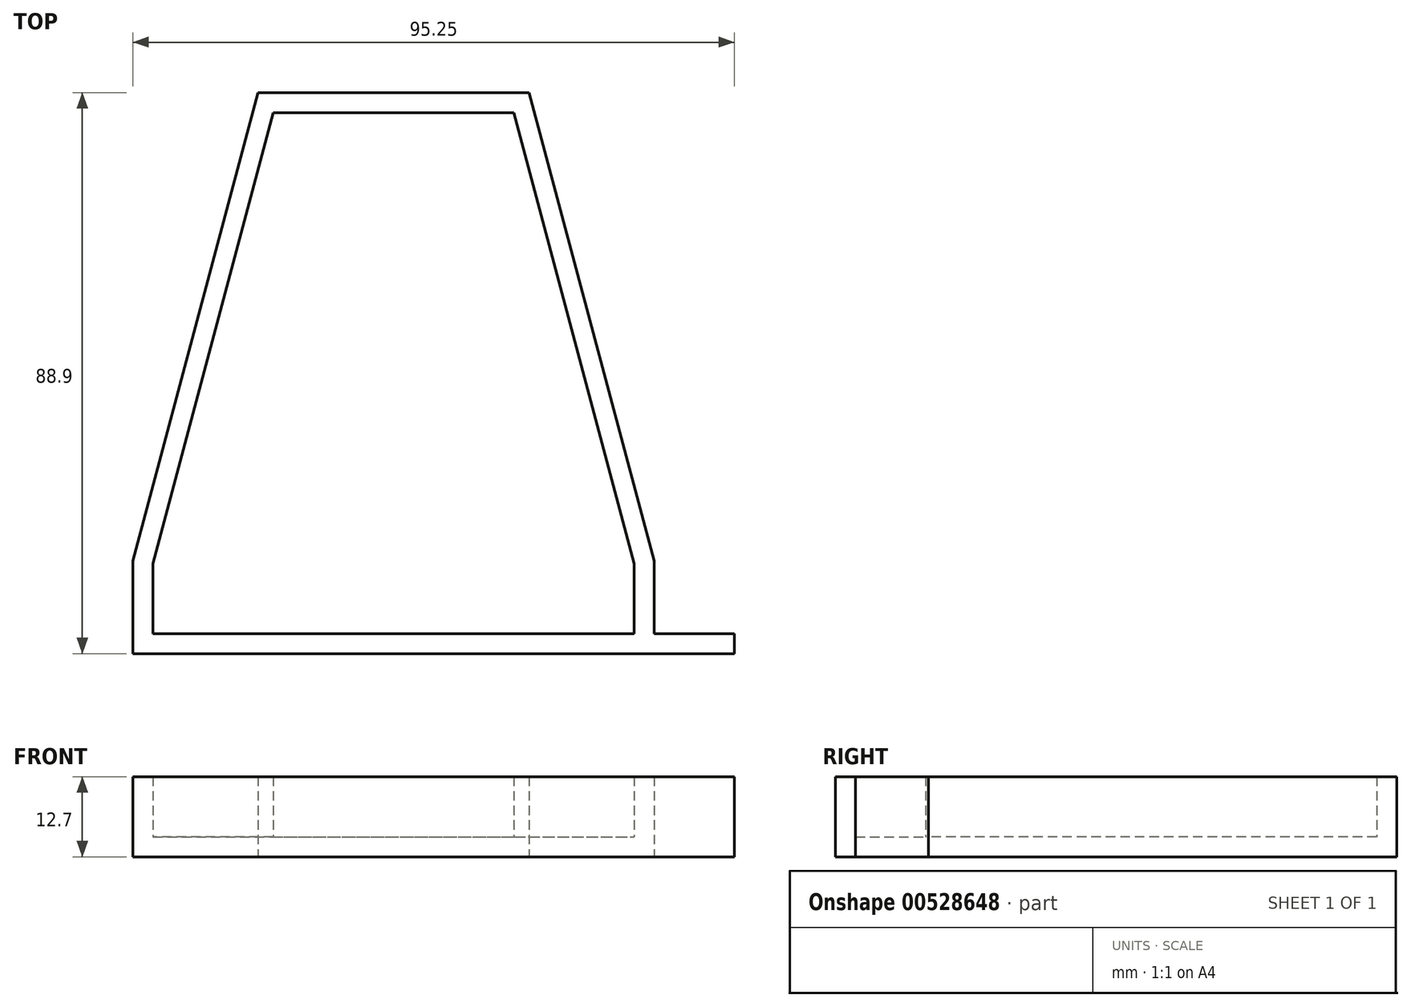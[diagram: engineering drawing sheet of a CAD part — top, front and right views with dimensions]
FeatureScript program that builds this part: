
annotation { "Feature Type Name" : "Feature", "Feature Type Description" : "" }
export const myFeature = defineFeature(function(context is Context, id is Id, definition is map)
    precondition{}
    {
        {
            var Q0;
            Q0=qCreatedBy(makeId("Top.planeOp"),FACE);
            var sketch = newSketch(context, id + "F0", { "sketchPlane" : qUnion([Q0])});
            skLineSegment(sketch, "E0.top", {"start": v(-38.1, -41.28) * mm, "end": v(38.1, -41.27) * mm});
            skLineSegment(sketch, "E1", {"start": v(38.1, -41.28) * mm, "end": v(38.1, -30.16) * mm});
            skLineSegment(sketch, "E2", {"start": v(19.05, 41.28) * mm, "end": v(38.1, -30.16) * mm});
            skLineSegment(sketch, "E3.MirrorCS", {"start": v(-19.05, 41.28) * mm, "end": v(-38.1, -30.16) * mm});
            skLineSegment(sketch, "E4.MirrorCS", {"start": v(-38.1, -41.28) * mm, "end": v(-38.1, -30.16) * mm});
            skLineSegment(sketch, "E5", {"start": v(-19.05, 41.27) * mm, "end": v(19.05, 41.28) * mm});
            skSolve(sketch);
        }
        {
            var Q0;
            Q0=makeQuery(id+"F0.imprint","IMPRINT",FACE,{"disambiguationData":[TD([[makeQuery(id+"F0.imprint","IMPRINT",EDGE,{"derivedFrom":sQuery(id+"F0.wireOp",EDGE,"E0.top")}),1.0]])]});
            var sketch = newSketch(context, id + "F1", { "sketchPlane" : qUnion([Q0])});
            skLineSegment(sketch, "E6.0", {"start": v(-21.49, 44.45) * mm, "end": v(-41.27, -29.75) * mm});
            skLineSegment(sketch, "E6.1", {"start": v(21.49, 44.45) * mm, "end": v(41.27, -29.75) * mm});
            skLineSegment(sketch, "E6.2", {"start": v(41.27, -44.45) * mm, "end": v(41.27, -29.75) * mm});
            skLineSegment(sketch, "E6.3", {"start": v(-21.49, 44.45) * mm, "end": v(21.49, 44.45) * mm});
            skLineSegment(sketch, "E6.4", {"start": v(-41.27, -44.45) * mm, "end": v(41.28, -44.45) * mm});
            skLineSegment(sketch, "E6.5", {"start": v(-41.27, -44.45) * mm, "end": v(-41.27, -29.75) * mm});
            skSolve(sketch);
        }
        {
            var Q0;
            Q0=makeQuery(id+"F0.imprint","IMPRINT",FACE,{"disambiguationData":[TD([[makeQuery(id+"F0.imprint","IMPRINT",EDGE,{"derivedFrom":sQuery(id+"F0.wireOp",EDGE,"E0.top")}),1.0]])]});
            extrude(context, id + "F2", {"entities" : qUnion([Q0]), "depth" : 3.17 * mm, "offsetDistance" : 25.4 * mm});
        }
        {
            var Q0;
            Q0=makeQuery(id+"F1.imprint","IMPRINT",FACE,{"disambiguationData":[TD([[makeQuery(id+"F1.imprint","IMPRINT",EDGE,{"derivedFrom":sQuery(id+"F1.wireOp",EDGE,"E6.0")}),1.0]])]});
            extrude(context, id + "F3", {"entities" : qUnion([Q0]), "operationType" : NewBodyOperationType.ADD, "depth" : 12.7 * mm, "offsetDistance" : 25.4 * mm});
        }
        {
            var Q0;
            Q0=makeQuery(id+"F3.opExtrude","SWEPT_FACE",FACE,{"disambiguationData":[OSD([sQuery(id+"F1.wireOp",EDGE,"E6.2")])]});
            var sketch = newSketch(context, id + "F4", { "sketchPlane" : qUnion([Q0])});
            skLineSegment(sketch, "E7.bottom", {"start": v(-44.45, 12.7) * mm, "end": v(-41.27, 12.7) * mm});
            skLineSegment(sketch, "E7.top", {"start": v(-44.45, 0) * mm, "end": v(-41.27, 0) * mm});
            skLineSegment(sketch, "E7.left", {"start": v(-44.45, 12.7) * mm, "end": v(-44.45, 0) * mm});
            skLineSegment(sketch, "E7.right", {"start": v(-41.27, 12.7) * mm, "end": v(-41.27, 0) * mm});
            skSolve(sketch);
        }
        {
            var Q0;
            Q0=makeQuery(id+"F4.imprint","IMPRINT",FACE,{"disambiguationData":[TD([[makeQuery(id+"F4.imprint","IMPRINT",EDGE,{"derivedFrom":sQuery(id+"F4.wireOp",EDGE,"E7.bottom")}),-1.0]])]});
            extrude(context, id + "F5", {"entities" : qUnion([Q0]), "operationType" : NewBodyOperationType.ADD, "depth" : 12.7 * mm, "offsetDistance" : 25.4 * mm});
        }
    });
